# Revit family: QF_Dietatec_GENIER-60-FS
name_source: partatom
category: Specialty Equipment
revit_build: Autodesk Revit 2016 (Build: 20150220_1215(x64)
units: mm (PartAtom-declared; Revit-internal decimal feet)

## family parameters
Always vertical = Yes
Cut with Voids When Loaded = No
OmniClass Number = 23.40.40.14
OmniClass Title = Food Service Equipment
Part Type = Normal
Room Calculation Point = No
Round Connector Dimension = Use Diameter
Shared = No
Work Plane-Based = No

## types (3) — shared parameters
Accessory = No
Apparent Power = 18500 VA
Assembly Code = E1090320
Cold Water Flow = 0.0 L/s
Cold Water Size = 13 mm
Cold Water Temperature Recommended = 0 °C
Conn Conduit = No
Cycle = 50 Hz
Depth Actual = 1274 mm  [stored 4.17979 ft]
Electric power = 18500 W
FL Amps = 27 A
Height Actual = 1080 mm  [stored 3.54331 ft]
Length Actual = 1170 mm  [stored 3.83858 ft]
Manufacturer = DIETATEC
Max Overcurrent Protection = 0 A
Min Ckt Ampacity = 0 A
Number of Poles = 3
Phase = 3
URL = www.dietatec.com
Volts = 400 V
Weight = 260.00 kg
zero-valued in all types: Cost

## per-type parameters (varying)
| type | Description | Model |
| 58051 | GO-CLASSIC NON-MIXER KETTLE, 60L | GO-CLASSIC 60 FS |
| 58031 | GENIER GO MIXER KETTLE, 60L | GENIER GO 60 FS |
| 58011 | GENIER ACE MIXER KETTLE, 60L | GENIER ACE 60 FS |

note: [stored X ft] marks values corroborated as IEEE doubles in the binary element streams (Revit-internal decimal feet)

## geometry (parser evidence)
native form markers: Sweep x3
no freeform markers — native parametric forms only
